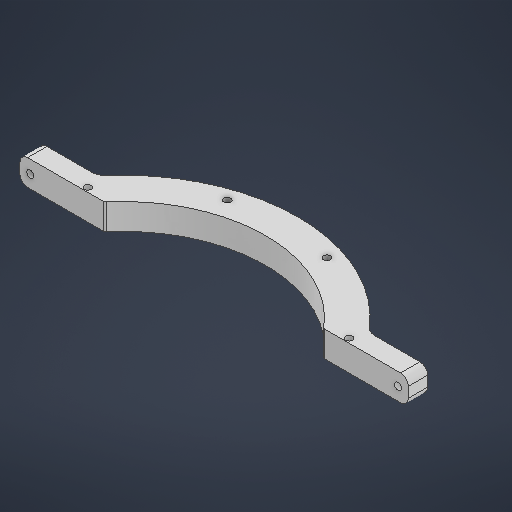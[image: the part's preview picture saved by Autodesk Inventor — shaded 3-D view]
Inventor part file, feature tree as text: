
AUTODESK INVENTOR PART (.ipt)
format: ipt  version: 2025 (Build 290162000, 162)  size: 302,592 bytes
history: native  units: in
note: dims shown in document units (in); Inventor stores cm internally (conversion verified against a paired STEP export)
features: sketch x6, fillet x4, extrude x3, hole x2, mirror x2, projected_geometry x1
ambient origin geometry x8: Origin, YZ Plane, XZ Plane, XY Plane, X Axis, Y Axis, Z Axis, Center Point
bodies: Solid1 (feature_tree)
feature tree (18):
  extrude  "Extrusion1"  Depth=8.6614in
  extrude  "Extrusion3"  Depth=0.7874in
  fillet  "Fillet1"  Radius=0.9843in
  fillet  "Fillet2"  Radius=0.5906in
  fillet  "Fillet3"  Radius=0.7874in
  hole  "Hole2"  [1 undecoded]
  mirror  "Mirror1"
  mirror  "Mirror2"
  hole  "Hole3"  [1 undecoded]
  extrude  "Extrusion7"  Depth=0.0787in
  fillet  "Fillet7"  Radius=0.3937in
  sketch  "Sketch1"  dims[d0=10.6299in d1=8.6614in]
  sketch  "Sketch4"  dims[d25=0.5906in d26=0.0in d27=0.0in]
  projected_geometry  "Projected Loop1"
  sketch  "Sketch5"  dims[d28=0.2362in d29=0.3937in]
  sketch  "Sketch7"  dims[d30=0.0787in]
  sketch  "Sketch11"  dims[d31=0.2165in d32=0.2362in d33=0.3465in d34=0.1969in d35=90.0deg d36=0.315in d37=0.8108in d38=0.315in d39=0.3937in d43=0.1969in d44=0.2362in d45=0.1575in d46=0.0787in d47=90.0deg d48=0.315in d49=0.8108in d50=5.0197in d57=0.3937in d61=0.0in d62=0.0in d63=0.0787in d69=9.8425in d75=0.2165in d76=3.937in d78=360.0deg]
  sketch  "Sketch Circular Pattern3"  dims[d2=0.7874in d3=0.0in d21=3.9469in d22=0.9843in d23=0.5906in d24=0.7874in]
note: 2 required parameter values undecoded (feature->parameter linkage not recoverable at this tier; creation-order binding heuristic only, values carry confidence <= 0.55)
